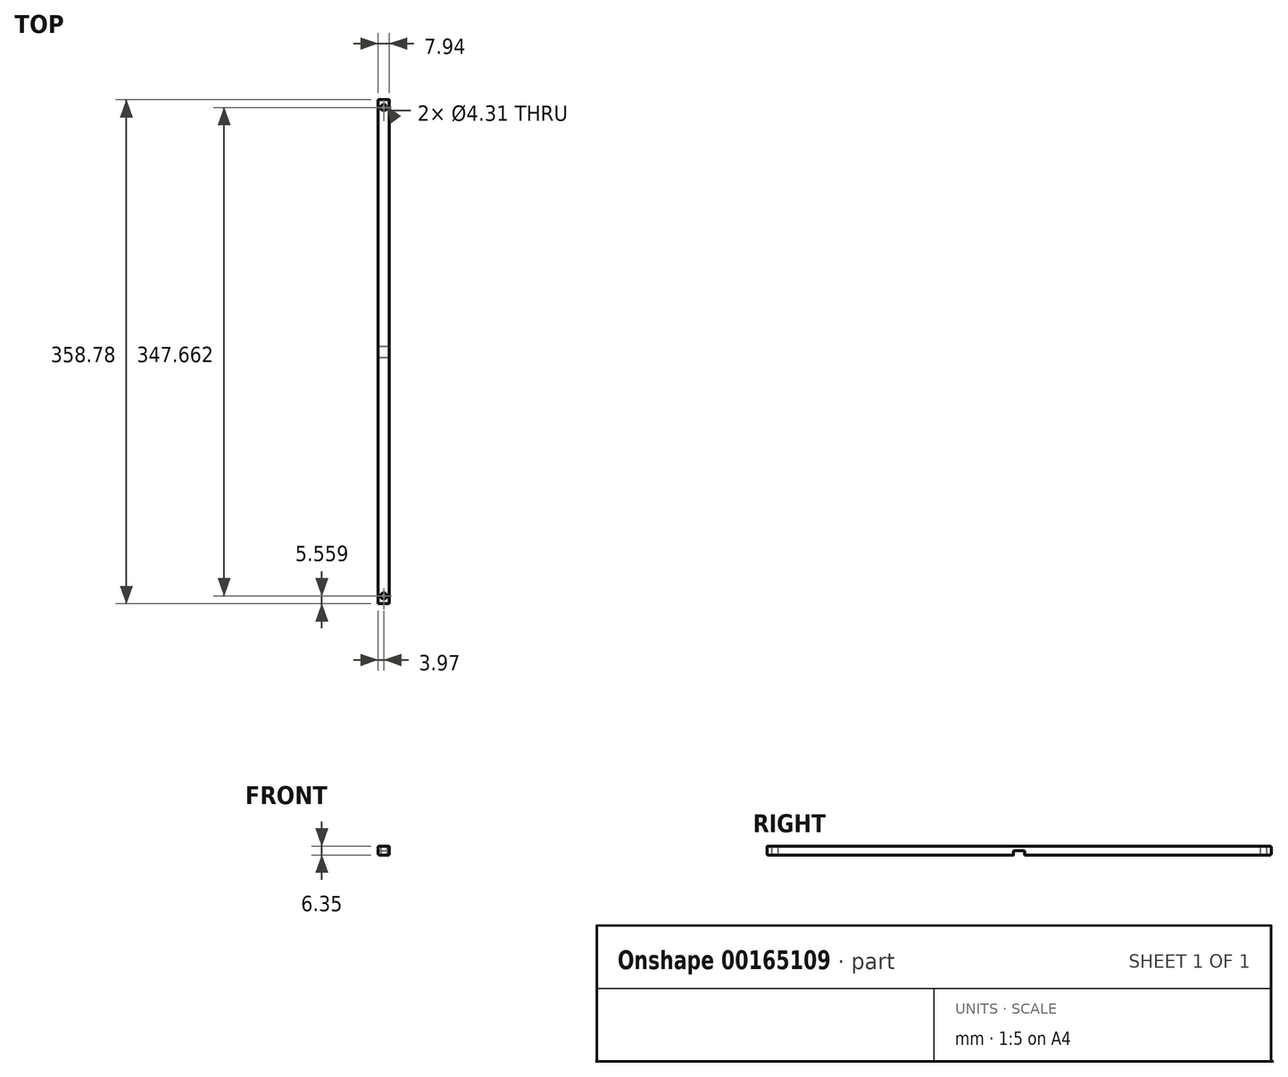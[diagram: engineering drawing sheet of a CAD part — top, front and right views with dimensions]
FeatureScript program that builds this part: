
annotation { "Feature Type Name" : "Feature", "Feature Type Description" : "" }
export const myFeature = defineFeature(function(context is Context, id is Id, definition is map)
    precondition{}
    {
        {
            var Q0;
            Q0=qCreatedBy(makeId("Top.planeOp"),FACE);
            var sketch = newSketch(context, id + "F0", { "sketchPlane" : qUnion([Q0])});
            skLineSegment(sketch, "E0.bottom", {"start": v(-3.97, 179.39) * mm, "end": v(3.97, 179.39) * mm});
            skLineSegment(sketch, "E0.top", {"start": v(-3.97, -179.39) * mm, "end": v(3.97, -179.39) * mm});
            skLineSegment(sketch, "E0.left", {"start": v(-3.97, 179.39) * mm, "end": v(-3.97, -179.39) * mm});
            skLineSegment(sketch, "E0.right", {"start": v(3.97, 179.39) * mm, "end": v(3.97, -179.39) * mm});
            skPoint(sketch, "E0.middle", {"position": v(0, 0) * mm});
            skLineSegment(sketch, "E1", {"start": v(0, -179.39) * mm, "end": v(0, -173.83) * mm, "construction": true});
            skLineSegment(sketch, "E2", {"start": v(0, -173.83) * mm, "end": v(0, 173.83) * mm, "construction": true});
            skLineSegment(sketch, "E3", {"start": v(0, 173.83) * mm, "end": v(0, 179.39) * mm, "construction": true});
            skCircle(sketch, "E4", {"center": v(0, -173.83) * mm, "radius": 2.15 * mm});
            skCircle(sketch, "E5", {"center": v(0, 173.83) * mm, "radius": 2.15 * mm});
            skSolve(sketch);
        }
        {
            var Q0;
            Q0 = qSketchRegion(id + "F0", true);
            extrude(context, id + "F1", {"entities" : qUnion([Q0]), "depth" : 6.35 * mm});
        }
        {
            var Q0;
            Q0=makeQuery(id+"F1.opExtrude","SWEPT_FACE",FACE,{"disambiguationData":[OSD([sQuery(id+"F0.wireOp",EDGE,"E0.right")])]});
            var sketch = newSketch(context, id + "F2", { "sketchPlane" : qUnion([Q0])});
            skLineSegment(sketch, "E6.bottom", {"start": v(-3.97, 0) * mm, "end": v(3.97, 0) * mm});
            skLineSegment(sketch, "E6.top", {"start": v(-3.97, 3.17) * mm, "end": v(3.97, 3.17) * mm});
            skLineSegment(sketch, "E6.left", {"start": v(-3.97, 0) * mm, "end": v(-3.97, 3.17) * mm});
            skLineSegment(sketch, "E6.right", {"start": v(3.97, 0) * mm, "end": v(3.97, 3.17) * mm});
            skSolve(sketch);
        }
        {
            var Q0;
            Q0 = qSketchRegion(id + "F2", true);
            var Q1;
            Q1=makeQuery(id+"F1.opExtrude","SWEPT_FACE",FACE,{"disambiguationData":[OSD([sQuery(id+"F0.wireOp",EDGE,"E0.left")])]});
            extrude(context, id + "F3", {"entities" : qUnion([Q0]), "operationType" : NewBodyOperationType.REMOVE, "endBound" : BoundingType.UP_TO_SURFACE, "oppositeDirection" : true, "endBoundEntityFace" : qUnion([Q1]), "depth" : 25.4 * mm});
        }
        {
            var Q0;
            Q0=makeQuery(id+"F1.opExtrude","CAP_EDGE",EDGE,{"disambiguationData":[OSD([sQuery(id+"F0.wireOp",EDGE,"E0.top")])],"isStart":true});
            var Q1;
            {var subQ0=sQuery(id+"F0.wireOp",EDGE,"E0.right");var subQ1=sQuery(id+"F0.wireOp",EDGE,"E0.top");Q1=makeQuery(id+"F3.boolean.opBoolean","SPLIT",EDGE,{"disambiguationData":[TD([makeQuery(id+"F1.opExtrude","SWEPT_FACE",FACE,{"disambiguationData":[OSD([subQ1])]})])],"derivedFrom":makeQuery(id+"F1.opExtrude","CAP_EDGE",EDGE,{"disambiguationData":[OSD([subQ0])],"isStart":true})});}
            var Q2;
            {var subQ0=sQuery(id+"F0.wireOp",EDGE,"E0.left");var subQ1=sQuery(id+"F0.wireOp",EDGE,"E0.top");Q2=makeQuery(id+"F3.boolean.opBoolean","SPLIT",EDGE,{"disambiguationData":[TD([makeQuery(id+"F1.opExtrude","SWEPT_FACE",FACE,{"disambiguationData":[OSD([subQ1])]})])],"derivedFrom":makeQuery(id+"F1.opExtrude","CAP_EDGE",EDGE,{"disambiguationData":[OSD([subQ0])],"isStart":true})});}
            var Q3;
            {var subQ0=sQuery(id+"F0.wireOp",EDGE,"E0.bottom");var subQ1=sQuery(id+"F0.wireOp",EDGE,"E0.left");Q3=makeQuery(id+"F3.boolean.opBoolean","SPLIT",EDGE,{"disambiguationData":[TD([makeQuery(id+"F1.opExtrude","SWEPT_FACE",FACE,{"disambiguationData":[OSD([subQ0])]})])],"derivedFrom":makeQuery(id+"F1.opExtrude","CAP_EDGE",EDGE,{"disambiguationData":[OSD([subQ1])],"isStart":true})});}
            var Q4;
            Q4=makeQuery(id+"F1.opExtrude","CAP_EDGE",EDGE,{"disambiguationData":[OSD([sQuery(id+"F0.wireOp",EDGE,"E0.bottom")])],"isStart":true});
            var Q5;
            {var subQ0=sQuery(id+"F0.wireOp",EDGE,"E0.bottom");var subQ1=sQuery(id+"F0.wireOp",EDGE,"E0.right");Q5=makeQuery(id+"F3.boolean.opBoolean","SPLIT",EDGE,{"disambiguationData":[TD([makeQuery(id+"F1.opExtrude","SWEPT_FACE",FACE,{"disambiguationData":[OSD([subQ0])]})])],"derivedFrom":makeQuery(id+"F1.opExtrude","CAP_EDGE",EDGE,{"disambiguationData":[OSD([subQ1])],"isStart":true})});}
            var Q6;
            Q6=makeQuery(id+"F1.opExtrude","CAP_EDGE",EDGE,{"disambiguationData":[OSD([sQuery(id+"F0.wireOp",EDGE,"E0.left")])],"isStart":false});
            var Q7;
            Q7=makeQuery(id+"F1.opExtrude","CAP_EDGE",EDGE,{"disambiguationData":[OSD([sQuery(id+"F0.wireOp",EDGE,"E0.top")])],"isStart":false});
            var Q8;
            Q8=makeQuery(id+"F1.opExtrude","CAP_EDGE",EDGE,{"disambiguationData":[OSD([sQuery(id+"F0.wireOp",EDGE,"E0.right")])],"isStart":false});
            var Q9;
            Q9=makeQuery(id+"F1.opExtrude","CAP_EDGE",EDGE,{"disambiguationData":[OSD([sQuery(id+"F0.wireOp",EDGE,"E0.bottom")])],"isStart":false});
            fillet(context, id + "F4", {"entities" : qUnion([Q0, Q1, Q2, Q3, Q4, Q5, Q6, Q7, Q8, Q9]), "radius" : 0.76 * mm, "tangentPropagation" : true, "allowEdgeOverflow" : false});
        }
    });
